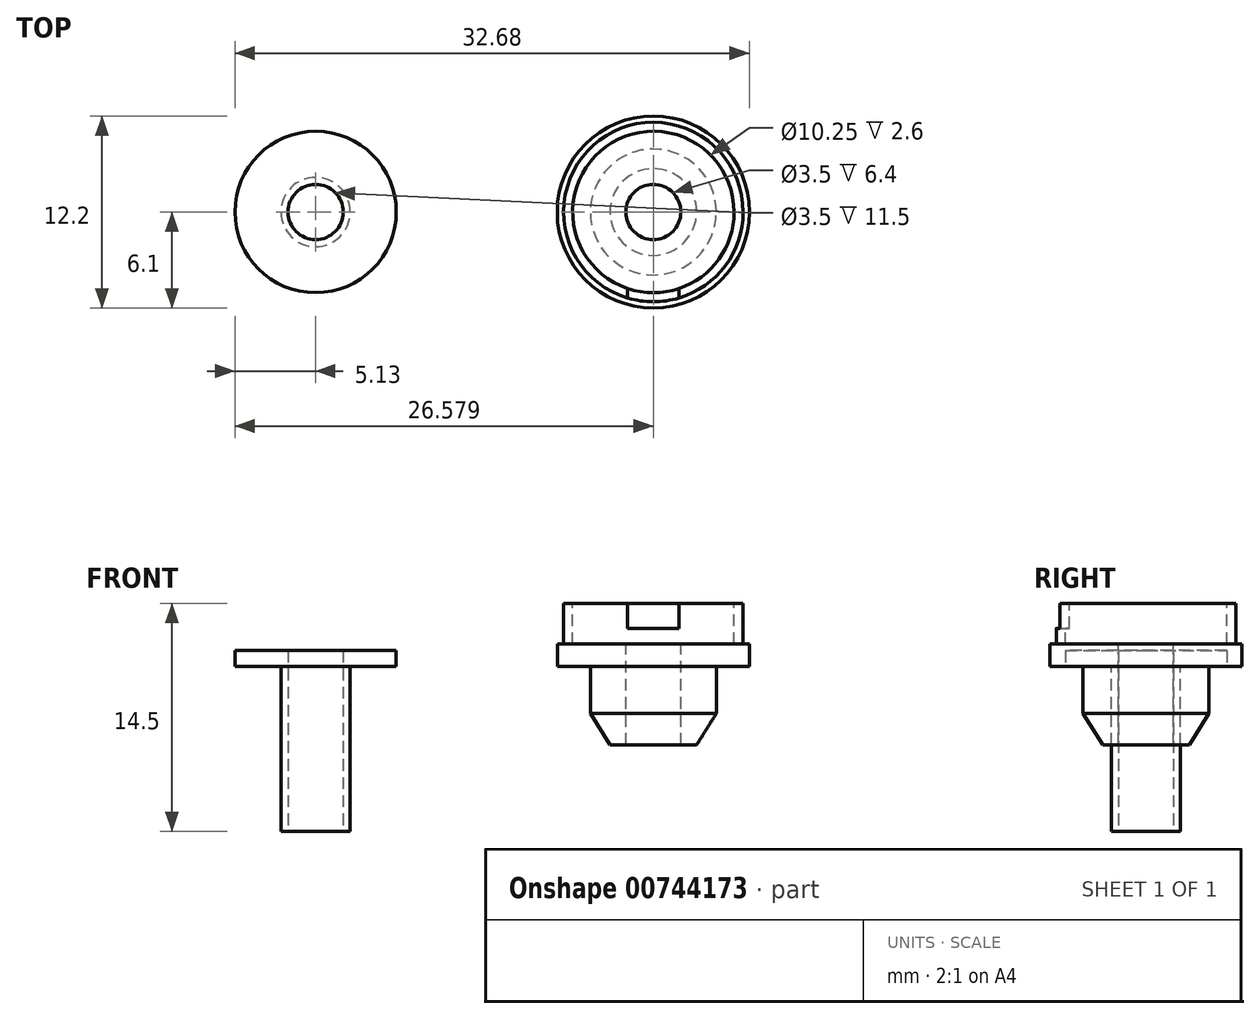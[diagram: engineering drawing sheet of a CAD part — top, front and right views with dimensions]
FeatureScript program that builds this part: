
annotation { "Feature Type Name" : "Feature", "Feature Type Description" : "" }
export const myFeature = defineFeature(function(context is Context, id is Id, definition is map)
    precondition{}
    {
        {
            var Q0;
            Q0=qCreatedBy(makeId("Top.planeOp"),FACE);
            var sketch = newSketch(context, id + "F0", { "sketchPlane" : qUnion([Q0])});
            skCircle(sketch, "E0", {"center": v(0, 0) * mm, "radius": 1.75 * mm});
            skCircle(sketch, "E1", {"center": v(0, 0) * mm, "radius": 5.12 * mm});
            skCircle(sketch, "E2", {"center": v(0, 0) * mm, "radius": 2.2 * mm});
            skSolve(sketch);
        }
        {
            var Q0;
            Q0=makeQuery(id+"F0.imprint","IMPRINT",FACE,{"disambiguationData":[TD([[makeQuery(id+"F0.imprint","IMPRINT",EDGE,{"derivedFrom":sQuery(id+"F0.wireOp",EDGE,"E0")}),-1.0]])]});
            var Q1;
            Q1=makeQuery(id+"F0.imprint","IMPRINT",FACE,{"disambiguationData":[TD([[makeQuery(id+"F0.imprint","IMPRINT",EDGE,{"derivedFrom":sQuery(id+"F0.wireOp",EDGE,"E1")}),1.0]])]});
            var Q2;
            Q2=sQuery(id+"F0.wireOp",EDGE,"E1");
            extrude(context, id + "F1", {"entities" : qUnion([Q0, Q1]), "surfaceEntities" : qUnion([Q2]), "depth" : 1 * mm, "offsetDistance" : 25 * mm});
        }
        {
            var Q0;
            Q0=makeQuery(id+"F0.imprint","IMPRINT",FACE,{"disambiguationData":[TD([[makeQuery(id+"F0.imprint","IMPRINT",EDGE,{"derivedFrom":sQuery(id+"F0.wireOp",EDGE,"E0")}),-1.0]])]});
            var Q1;
            Q1=sQuery(id+"F0.wireOp",EDGE,"E2");
            extrude(context, id + "F2", {"entities" : qUnion([Q0]), "operationType" : NewBodyOperationType.ADD, "surfaceEntities" : qUnion([Q1]), "oppositeDirection" : true, "depth" : 10.5 * mm, "offsetDistance" : 25 * mm});
        }
        {
            var Q0;
            Q0=qCreatedBy(makeId("Front.planeOp"),FACE);
            var sketch = newSketch(context, id + "F3", { "sketchPlane" : qUnion([Q0])});
            skLineSegment(sketch, "E3", {"start": v(25.45, 0) * mm, "end": v(27.55, 0) * mm});
            skLineSegment(sketch, "E4", {"start": v(27.55, 0) * mm, "end": v(27.55, 1.4) * mm});
            skLineSegment(sketch, "E5", {"start": v(27.55, 1.4) * mm, "end": v(27.15, 1.4) * mm});
            skLineSegment(sketch, "E6", {"start": v(27.15, 1.4) * mm, "end": v(27.15, 4) * mm});
            skLineSegment(sketch, "E7", {"start": v(27.15, 4) * mm, "end": v(26.57, 4) * mm});
            skLineSegment(sketch, "E8", {"start": v(26.57, 4) * mm, "end": v(26.57, 1.4) * mm});
            skLineSegment(sketch, "E9", {"start": v(26.57, 1.4) * mm, "end": v(23.2, 1.4) * mm});
            skLineSegment(sketch, "E10", {"start": v(23.2, 1.4) * mm, "end": v(23.2, -5) * mm});
            skLineSegment(sketch, "E11", {"start": v(23.2, -5) * mm, "end": v(24.2, -5) * mm});
            skLineSegment(sketch, "E12", {"start": v(24.2, -5) * mm, "end": v(25.45, -3) * mm});
            skLineSegment(sketch, "E13", {"start": v(25.45, 0) * mm, "end": v(25.45, -3) * mm});
            skLineSegment(sketch, "E14", {"start": v(21.45, 5.18) * mm, "end": v(21.45, -6.53) * mm, "construction": true});
            skSolve(sketch);
        }
        {
            var Q0;
            Q0=makeQuery(id+"F3.imprint","IMPRINT",FACE,{"disambiguationData":[TD([[makeQuery(id+"F3.imprint","IMPRINT",EDGE,{"derivedFrom":sQuery(id+"F3.wireOp",EDGE,"E3")}),1.0]])]});
            var Q1;
            Q1=sQuery(id+"F3.wireOp",EDGE,"E6");
            var Q2;
            Q2=sQuery(id+"F3.wireOp",EDGE,"E3");
            var Q3;
            Q3=sQuery(id+"F3.wireOp",EDGE,"E9");
            var Q4;
            Q4=sQuery(id+"F3.wireOp",EDGE,"E8");
            var Q5;
            Q5=sQuery(id+"F3.wireOp",EDGE,"E13");
            var Q6;
            Q6=sQuery(id+"F3.wireOp",EDGE,"E12");
            var Q7;
            Q7=sQuery(id+"F3.wireOp",EDGE,"E10");
            var Q8;
            Q8=sQuery(id+"F3.wireOp",EDGE,"E11");
            var Q9;
            Q9=sQuery(id+"F3.wireOp",EDGE,"E4");
            var Q10;
            Q10=sQuery(id+"F3.wireOp",EDGE,"E7");
            var Q11;
            Q11=sQuery(id+"F3.wireOp",EDGE,"E5");
            var Q12;
            Q12=sQuery(id+"F3.wireOp",EDGE,"E14");
            revolve(context, id + "F4", {"surfaceOperationType" : NewSurfaceOperationType.NEW, "entities" : qUnion([Q0]), "surfaceEntities" : qUnion([Q1, Q2, Q3, Q4, Q5, Q6, Q7, Q8, Q9, Q10, Q11]), "axis" : qUnion([Q12]), "revolveType" : RevolveType.FULL});
        }
        {
            var Q0;
            Q0=qCreatedBy(makeId("Front.planeOp"),FACE);
            var sketch = newSketch(context, id + "F5", { "sketchPlane" : qUnion([Q0])});
            skLineSegment(sketch, "E15.top", {"start": v(19.82, 2.4) * mm, "end": v(23.07, 2.4) * mm});
            skLineSegment(sketch, "E15.left", {"start": v(19.82, 4) * mm, "end": v(19.82, 2.4) * mm});
            skLineSegment(sketch, "E15.right", {"start": v(23.07, 4) * mm, "end": v(23.07, 2.4) * mm});
            skLineSegment(sketch, "E16", {"start": v(19.82, 4) * mm, "end": v(23.07, 4) * mm});
            skSolve(sketch);
        }
        {
            var Q0;
            Q0=makeQuery(id+"F5.imprint","IMPRINT",FACE,{"disambiguationData":[TD([[makeQuery(id+"F5.imprint","IMPRINT",EDGE,{"derivedFrom":sQuery(id+"F5.wireOp",EDGE,"E15.top")}),1.0]])]});
            var Q1;
            Q1=sQuery(id+"F5.wireOp",EDGE,"E15.right");
            var Q2;
            Q2=sQuery(id+"F5.wireOp",EDGE,"E16");
            var Q3;
            Q3=sQuery(id+"F5.wireOp",EDGE,"E15.left");
            var Q4;
            Q4=sQuery(id+"F5.wireOp",EDGE,"E15.top");
            extrude(context, id + "F6", {"entities" : qUnion([Q0]), "operationType" : NewBodyOperationType.REMOVE, "surfaceEntities" : qUnion([Q1, Q2, Q3, Q4]), "endBound" : BoundingType.THROUGH_ALL, "depth" : 25 * mm, "offsetDistance" : 25 * mm});
        }
    });
